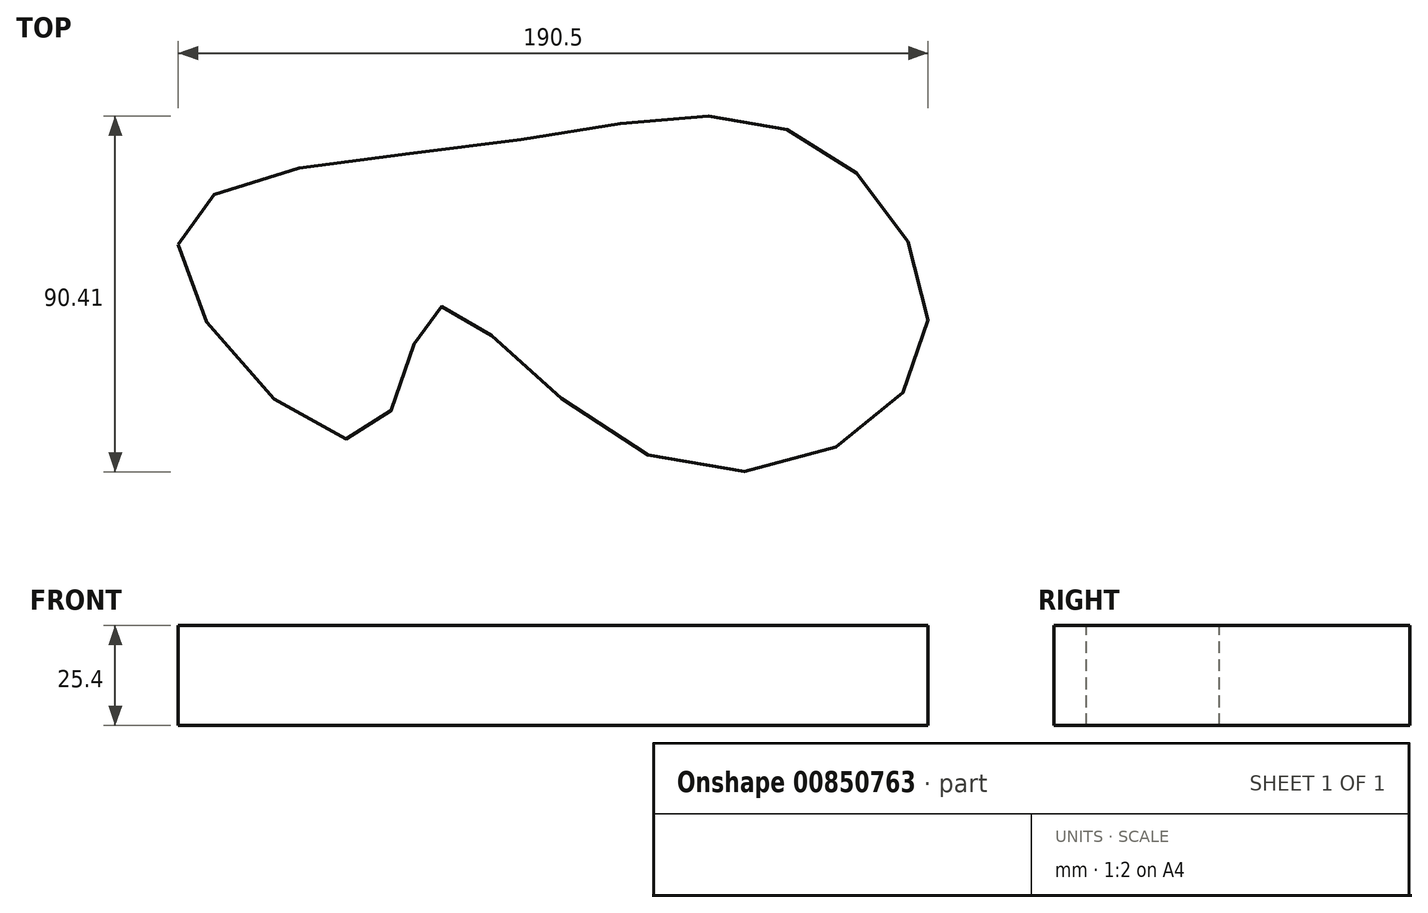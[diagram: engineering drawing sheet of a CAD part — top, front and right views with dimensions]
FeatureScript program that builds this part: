
annotation { "Feature Type Name" : "Feature", "Feature Type Description" : "" }
export const myFeature = defineFeature(function(context is Context, id is Id, definition is map)
    precondition{}
    {
        {
            var Q0;
            Q0=qCreatedBy(makeId("Top.planeOp"),FACE);
            var sketch = newSketch(context, id + "F0", { "sketchPlane" : qUnion([Q0])});
            skFitSpline(sketch, "E0", {"points": [v(-126.56, 28.2) * mm, v(-79.26, -20.93) * mm, v(-61.73, 11.76) * mm, v(-4.36, -26.46) * mm, v(62.53, 0) * mm, v(33.4, 55.04) * mm, v(-50.38, 53.26) * mm, v(-126.56, 28.2) * mm]});
            skSolve(sketch);
        }
        {
            var Q0;
            Q0=sQuery(id+"F0.wireOp",EDGE,"E0");
            extrude(context, id + "F1", {"bodyType" : ToolBodyType.SURFACE, "surfaceEntities" : qUnion([Q0]), "depth" : 25.4 * mm, "offsetDistance" : 25.4 * mm});
        }
    });
